# Revit family: FORM-20-SM-CM_no_ESC_Lens_Lighting_Non-Hosted_R20
name_source: partatom
category: Lighting Fixtures
units: mm (PartAtom-declared; Revit-internal decimal feet)

## family parameters
Always vertical = Yes
Cut with Voids When Loaded = No
Light Source = Yes
OmniClass Number = 23.80.70.00
OmniClass Title = Lighting
Part Type = Normal
Room Calculation Point = No
Round Connector Dimension = Use Diameter
Shared = No
Work Plane-Based = No

## types (18) — shared parameters
Charging Method = Intelligent Current Limited Constant Voltage
Color Filter = 16777215
Construction = Cast Aluminium Box with PC/Aluminium Extrusion Blade
Diffuser = Polycarbonate
Dimensions (L x W x H) = 220 x 18 x 110
Dimming Lamp Color Temperature Shift = <None>
Earth Leakage = 0.35
Emit Shape Visible in Rendering = No
IK Rating = IK03
IP Rating = IP20
Inrush Current (Max) = 10A<144µs
Lamp = 18 x LED, 170,000 hours
Manufacturer = Clevertronics
Mounting = Surface Ceiling Mount, Double Sided
Operating Mode = Maintained
Operating Temperature = 0 ºC - 40ºC
Operating Voltage = 220-240V~ 50Hz
Photometric Web File = generic
Power Factor = 0.28 (Standby, Maintained), 0.42 (Max)
Tilt Angle = 90.00°
Viewing Distance = 20m
zero-valued in all types: Default Elevation

## per-type parameters (varying)
| type | Battery | Battery Type | Description | MIC Number | Model | Power Consumption | Power Consumption (Standby - Lamp Off) | Replacement Battery | Replacement Emergency Driver | Replacement Item | Supply Current | Testing System | Type Comments | Weight |
| FORM-20-SM-CM-RS-LP-HVG | 3.2V 1100mAh | Lithium Iron Phosphate | Form 20m Exit, Surface Ceiling Mount, Rod Suspended, CLP, Zoneworks XT Hive, Picto All, Double Sided, Brushed Aluminium Frame | UKA02810190001 | FORM-20-SM-CM-RS-LP-HVG | 3.6W | 1.5W | 1550150 - BATT:LP 3.2V 1100mAh 70mm lead, no BRKT | UKM02870300001 - CLEDDRV2CH-RR-2C170-6C30-15-CKIT-HVGEXTA, LED Driver, Control Only, RR, 6C30, LP, HVGEXTA | 8003345 - PCA: 2.4Ghz RF Node CT10748-A1 Ext Ant Horizontal | 19.91 (Standby, Maintained), 35.60 (Max) - (mA) | Zoneworks XTHIVE (RF) | Form 20M Exit, Surf CM RS, LP, ZW HT Hive, Alm | 1.30 |
| FORM-20-SM-CM-RS-LP-DALI | 3.2V 1100mAh | Lithium Iron Phosphate | Form 20m Exit, Surface Ceiling Mount, Rod Suspended, CLP, DALI Emergency, Picto All, Double Sided, Brushed Aluminium Frame | UKA02210200002 | FORM-20-SM-CM-RS-LP-DALI | 3.6W | 1.5W | 1550150 - BATT:LP 3.2V 1100mAh 70mm lead, no BRKT | UKM02270080002 - CLEDDRV2CH-RR-2C170-6C30-15-CKIT-DALI, LED Driver, Control Only, RR, 6C30, LP, Dali Reg | 8003068 - PCA: CT10629-A4 DALI Horizontal - FORM | 19.91 (Standby, Maintained), 35.60 (Max) - (mA) | DALI Registered | Form 20M Exit, Surf CM RS, LP, Dali Reg, Alm | 1.30 |
| FORM-20-SM-CM-RS-LP | 3.2V 1100mAh | Lithium Iron Phosphate | Form 20m Exit, Surface Ceiling Mount, Rod Suspended, CLP, Clevertest Plus, Picto All, Double Sided, Brushed Aluminium Frame | UKA02310200001 | FORM-20-SM-CM-RS-LP | 3.3W | 1.2W | 1550150 - BATT:LP 3.2V 1100mAh 70mm lead, no BRKT | UKM02370210001 - CLEDDRV2CH-RR-2C170-6C30-15-CKIT, LED Driver, Control Only, RR, 6C30, LP, CTP |  | 18.61 (Standby, Maintained), 34.30 (Max) - (mA) | Clevertest Plus Enabled (Not Activated By Default) | Form 20M Exit, Surf CM RS, LP, CTP, Alm | 1.30 |
| FORM-20-SM-CM-RS-L10-HVG | 3.3V 2500mAh | Lithium Nanophosphate | Form 20m Exit, Surface Ceiling Mount, Rod Suspended, L10 Nanophosphate, Zoneworks XT Hive, Picto All, Double Sided, Brushed Aluminium Frame | UKA01810260001 | FORM-20-SM-CM-RS-L10-HVG | 3.6W | 1.5W | 1530050 - BATT:L10 3.3V 2.5AH 70mm lead, no BRKT | UKM01870370001 - LLEDDRV2CH-RR-2C170-6C30-15-CKIT-HVGEXTA, LED Driver, Control Only, RR, 6C30, L10, HVGEXTA | 8003345 - PCA: 2.4Ghz RF Node CT10748-A1 Ext Ant Horizontal | 19.91 (Standby, Maintained), 35.60 (Max) - (mA) | Zoneworks XT HIVE (RF) | Form 20M Exit, Surf CM RS, L10, ZW HT Hive, Alm | 1.30 |
| FORM-20-SM-CM-RS-L10-DALI | 3.3V 2500mAh | Lithium Nanophosphate | Form 20m Exit, Surface Ceiling Mount, Rod Suspended, L10 Nanophosphate, DALI Emergency, Picto All, Double Sided, Brushed Aluminium Frame | UKA01210200002 | FORM-20-SM-CM-RS-L10-DALI | 3.6W | 1.5W | 1530050 - BATT:L10 3.3V 2.5AH 70mm lead, no BRKT | UKM01270080002 LLEDDRV2CH-RR-2C170-6C30-15-CKIT-DALI, LED Driver, Control Only, RR, 6C30, L10, Dali Reg | 8003068 - PCA: CT10629-A4 DALI Horizontal - FORM | 19.91 (Standby, Maintained), 35.60 (Max) - (mA) | DALI Registered | Form 20M Exit, Surf CM RS, L10, Dali Reg, Alm | 1.30 |
| FORM-20-SM-CM-RS-L10 | 3.3V 2500mAh | Lithium Nanophosphate | Form 20m Exit, Surface Ceiling Mount, Rod Suspended, L10 Nanophosphate, Clevertest Plus, Picto All, Double Sided, Brushed Aluminium Frame | UKA01310170001 | FORM-20-SM-CM-RS-L10 | 3.3W | 1.2W | 1530050 - BATT:L10 3.3V 2.5AH 70mm lead, no BRKT | UKM01370300001- LLEDDRV2CH-RR-2C170-6C30-15-CKIT, LED Driver, Control Only, RR, 6C30, L10, CTP |  | 18.61 (Standby, Maintained), 34.30 (Max) - (mA) | Clevertest Plus Enabled (Not Activated By Default) | Form 20M Exit, Surf CM RS, L10, CTP, Alm | 1.30 |
| FORM-20-SM-CM-LP-HVG | 3.2V 1100mAh | Lithium Iron Phosphate | Form 20m Exit, Surface Ceiling Mount, CLP, Zoneworks XT Hive, Picto All, Double Sided, Brushed Aluminium Frame | UKA02810200001 | FORM-20-SM-CM-LP-HVG
FORM-20-SM-CM-LP-HVG | 3.6W | 1.5W | 1550150 - BATT:LP 3.2V 1100mAh 70mm lead, no BRKT | UKM02870300001 - CLEDDRV2CH-RR-2C170-6C30-15-CKIT-HVGEXTA, LED Driver, Control Only, RR, 6C30, LP, HVGEXTA | 8003345 - PCA: 2.4Ghz RF Node CT10748-A1 Ext Ant Horizontal | 19.91 (Standby, Maintained), 35.60 (Max) - (mA) | Zoneworks XTHIVE (RF) | Form 20M Exit, Surf CM, CLP, ZW HT Hive, Alm | 0.80kg |
| FORM-20-SM-CM-CS-LP | 3.2V 1100mAh | Lithium Iron Phosphate | Form 20m Exit, Surface Ceiling Mount, Cable Suspended, CLP, Clevertest Plus, Picto All, Double Sided, Brushed Aluminium Frame | UKA02310190001 | FORM-20-SM-CM-CS-LP | 3.3W | 1.2W | 1550150 - BATT:LP 3.2V 1100mAh 70mm lead, no BRKT | UKM02370210001 - CLEDDRV2CH-RR-2C170-6C30-15-CKIT, LED Driver, Control Only, RR, 6C30, LP, CTP |  | 18.61 (Standby, Maintained), 34.30 (Max) - (mA) | Clevertest Plus Enabled (Not Activated By Default) | Form 20M Exit, Surf CM CS, LP, CTP, Alm | 0.90 |
| FORM-20-SM-CM-CS-L10-DALI | 3.3V 2500mAh | Lithium Nanophosphate | Form 20m Exit, Surface Ceiling Mount, Cable Suspended, L10 Nanophosphate, DALI Emergency, Picto All, Double Sided, Brushed Aluminium Frame | UKA01210190002 | FORM-20-SM-CM-CS-L10-DALI | 3.6W | 1.5W | 1530050 - BATT:L10 3.3V 2.5AH 70mm lead, no BRKT | UKM01270080002 - LLEDDRV2CH-RR-2C170-6C30-15-CKIT-DALI, LED Driver, Control Only, RR, 6C30, L10, Dali Reg | 8003068 - PCA: CT10629-A4 DALI Horizontal - FORM | 19.91 (Standby, Maintained), 35.60 (Max) - (mA) | DALI Registered | Form 20M Exit, Surf CM CS, L10, Dali Reg, Alm | 0.90 |
| FORM-20-SM-CM-L10-DALI | 3.3V 2500mAh | Lithium Nanophosphate | Form 20m Exit, Surface Ceiling Mount, L10 Nanophosphate, DALI Emergency, Picto All, Double Sided, Brushed Aluminium Frame | UKA01210210002 | FORM-20-SM-CM-L10-DALI | 3.6W | 1.5W | 1530050 - BATT:L10 3.3V 2.5AH 70mm lead, no BRKT | UKM01270080002 - LLEDDRV2CH-RR-2C170-6C30-15-CKIT-DALI, LED Driver, Control Only, RR, 6C30, L10, Dali Reg | 8003068 - PCA: CT10629-A4 DALI Horizontal - FORM | 19.91 (Standby, Maintained), 35.60 (Max) - (mA) | DALI Registered | Form 20M Exit, Surf CM, L10, Dali Reg, Alm | 0.80 |
| FORM-20-SM-CM-L10 | 3.3V 2500mAh | Lithium Nanophosphate | Form 20m Exit, Surface Ceiling Mount, L10 Nanophosphate, Clevertest Plus, Picto All, Double Sided, Brushed Aluminium Frame | UKA01310160001 | FORM-20-SM-CM-L10 | 3.3W | 1.2W | 1530050 - BATT:L10 3.3V 2.5AH 70mm lead, no BRKT | UKM01370300001 - LLEDDRV2CH-RR-2C170-6C30-15-CKIT, LED Driver, Control Only, RR, 6C30, L10, CTP |  | 18.61 (Standby, Maintained), 34.30 (Max) - (mA) | Clevertest Plus Enabled (Not Activated By Default) | Form 20M Exit, Surf CM, L10, CTP, Alm | 0.80 |
| FORM-20-SM-CM-CS-L10 | 3.3V 2500mAh | Lithium Nanophosphate | Form 20m Exit, Surface Ceiling Mount, Cable Suspended, L10 Nanophosphate, Clevertest Plus, Picto All, Double Sided, Brushed Aluminium Frame | UKA01310180001 | FORM-20-SM-CM-CS-L10 | 3.3W | 1.2W | 1530050 - BATT:L10 3.3V 2.5AH 70mm lead, no BRKT | UKM01370300001 - LLEDDRV2CH-RR-2C170-6C30-15-CKIT, LED Driver, Control Only, RR, 6C30, L10, CTP |  | 18.61 (Standby, Maintained), 34.30 (Max) - (mA) | Clevertest Plus Enabled (Not Activated By Default) | Form 20M Exit, Surf CM CS, L10, CTP, Alm | 0.90 |
| FORM-20-SM-CM-CS-L10-HVG | 3.3V 2500mAh | Lithium Nanophosphate | Form 20m Exit, Surface Ceiling Mount, Cable Suspended, L10 Nanophosphate, Zoneworks XT Hive, Picto All, Double Sided, Brushed Aluminium Frame | UKA01810250001 | FORM-20-SM-CM-CS-L10-HVG | 3.6W | 1.5W | 1530050 - BATT:L10 3.3V 2.5AH 70mm lead, no BRKT | UKM01870370001 - LLEDDRV2CH-RR-2C170-6C30-15-CKIT-HVGEXTA, LED Driver, Control Only, RR, 6C30, L10, HVGEXTA | 8003345 - PCA: 2.4Ghz RF Node CT10748-A1 Ext Ant Horizontal | 19.91 (Standby, Maintained), 35.60 (Max) - (mA) | Zoneworks XT HIVE (RF) | Form 20M Exit, Surf CM CS, L10, ZW HT Hive, Alm | 0.90 |
| FORM-20-SM-CM-L10-HVG | 3.3V 2500mAh | Lithium Nanophosphate | Form 20m Exit, Surface Ceiling Mount, L10 Nanophosphate, Zoneworks XT Hive, Picto All, Double Sided, Brushed Aluminium Frame | UKA01810270001 | FORM-20-SM-CM-L10-HVG | 3.6W | 1.5W | 1530050 - BATT:L10 3.3V 2.5AH 70mm lead, no BRKT | UKM01870370001 - LLEDDRV2CH-RR-2C170-6C30-15-CKIT-HVGEXTA, LED Driver, Control Only, RR, 6C30, L10, HVGEXTA | 8003345 - PCA: 2.4Ghz RF Node CT10748-A1 Ext Ant Horizontal | 19.91 (Standby, Maintained), 35.60 (Max) - (mA) | Zoneworks XT HIVE (RF) | Form 20M Exit, Surf CM, L10, ZW HT Hive, Alm | 0.80 |
| FORM-20-SM-CM-CS-LP-DALI | 3.2V 1100mAh | Lithium Iron Phosphate | Form 20m Exit, Surface Ceiling Mount, Cable Suspended, CLP, DALI Emergency, Picto All, Double Sided, Brushed Aluminium Frame | UKA02210190002 | FORM-20-SM-CM-CS-LP-DALI | 3.6W | 1.5W | 1550150 - BATT:LP 3.2V 1100mAh 70mm lead, no BRKT | UKM02270080002 - CLEDDRV2CH-RR-2C170-6C30-15-CKIT-DALI, LED Driver, Control Only, RR, 6C30, LP, Dali Reg | 8003068 - PCA: CT10629-A4 DALI Horizontal - FORM | 19.91 (Standby, Maintained), 35.60 (Max) - (mA) | DALI Registered | Form 20M Exit, Surf CM CS, LP, Dali Reg, Alm | 0.90 |
| FORM-20-SM-CM-LP-DALI | 3.2V 1100mAh | Lithium Iron Phosphate | Form 20m Exit, Surface Ceiling Mount, CLP, DALI Emergency, Picto All, Double Sided, Brushed Aluminium Frame | UKA02210210002 | FORM-20-SM-CM-LP-DALI
FORM-20-SM-CM-LP-HVG | 3.6W | 1.5W | 1550150 - BATT:LP 3.2V 1100mAh 70mm lead, no BRKT | UKM02270080002 - CLEDDRV2CH-RR-2C170-6C30-15-CKIT-DALI, LED Driver, Control Only, RR, 6C30, LP, Dali Reg | 8003068 - PCA: CT10629-A4 DALI Horizontal - FORM | 19.91 (Standby, Maintained), 35.60 (Max) - (mA) | DALI Registered | Form 20M Exit, Surf CM, CLP, Dali Reg, Alm | 1.30 |
| FORM-20-SM-CM-LP | 3.2V 1100mAh | Lithium Iron Phosphate | Form 20m Exit, Surface Ceiling Mount, CLP, Clevertest Plus, Picto All, Double Sided, Brushed Aluminium Frame | UKA02310140001 | FORM-20-SM-CM-LP
FORM-20-SM-CM-LP-HVG | 3.3W | 1.2W | 1550150 - BATT:LP 3.2V 1100mAh 70mm lead, no BRKT | UKM02370210001 - CLEDDRV2CH-RR-2C170-6C30-15-CKIT, LED Driver, Control Only, RR, 6C30, LP, CTP |  | 18.61 (Standby, Maintained), 34.30 (Max) - (mA) | Clevertest Plus Enabled (Not Activated By Default) | Form 20M Exit, Surf CM, CLP, CTP, Alm | 0.80 |
| FORM-20-SM-CM-CS-LP-HVG | 3.2V 1100mAh | Lithium Iron Phosphate | Form 20m Exit, Surface Ceiling Mount, Cable Suspended, CLP, Zoneworks XT Hive, Picto All, Double Sided, Brushed Aluminium Frame | UKA02810180001 | FORM-20-SM-CM-CS-LP-HVG | 3.6W | 1.5W | 1550150 - BATT:LP 3.2V 1100mAh 70mm lead, no BRKT | UKM02870300001 - CLEDDRV2CH-RR-2C170-6C30-15-CKIT-HVGEXTA, LED Driver, Control Only, RR, 6C30, LP, HVGEXTA | 8003345 - PCA: 2.4Ghz RF Node CT10748-A1 Ext Ant Horizontal | 19.91 (Standby, Maintained), 35.60 (Max) - (mA) | Zoneworks XTHIVE (RF) | Form 20M Exit, Surf CM CS, LP, ZW HT Hive, Alm | 0.90 |

## geometry (parser evidence)
native form markers: Extrusion x20, Sweep x3
no freeform markers — native parametric forms only
